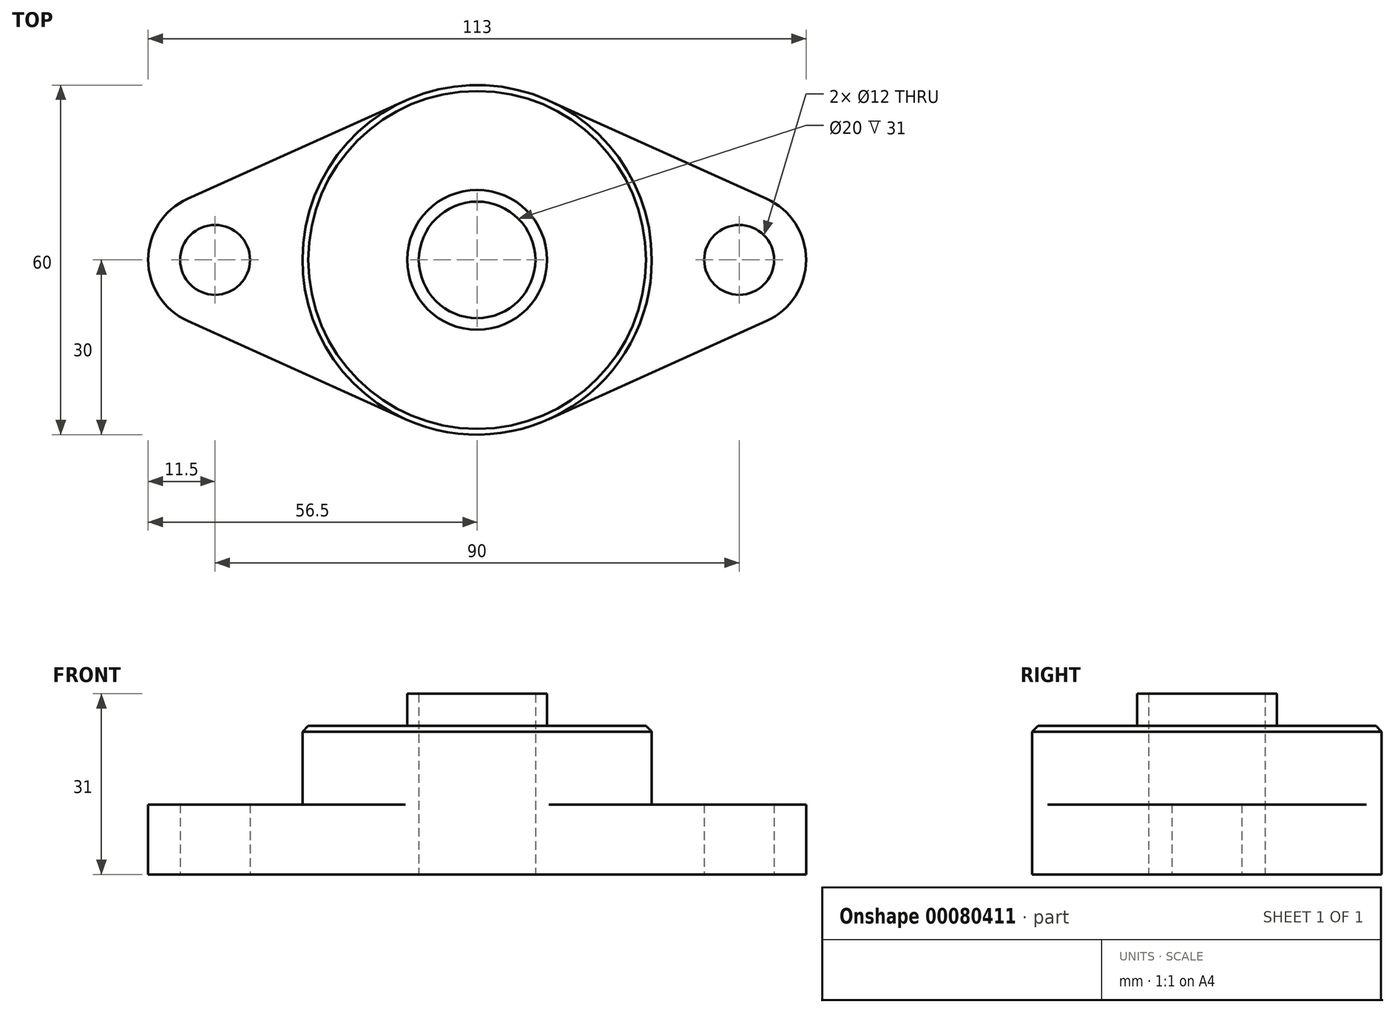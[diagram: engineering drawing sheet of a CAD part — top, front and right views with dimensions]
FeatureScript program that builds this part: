
annotation { "Feature Type Name" : "Feature", "Feature Type Description" : "" }
export const myFeature = defineFeature(function(context is Context, id is Id, definition is map)
    precondition{}
    {
        {
            var Q0;
            Q0=qCreatedBy(makeId("Top.planeOp"),FACE);
            var sketch = newSketch(context, id + "F0", { "sketchPlane" : qUnion([Q0])});
            skCircle(sketch, "E0", {"center": v(0, 0) * mm, "radius": 10 * mm});
            skArc(sketch, "E1", {"start": v(-49.73, 10.48) * mm, "mid": v(-56.5, 0) * mm, "end": v(-49.73, -10.48) * mm});
            skArc(sketch, "E2", {"start": v(-12.33, -27.35) * mm, "mid": v(0, -30) * mm, "end": v(12.33, -27.35) * mm});
            skLineSegment(sketch, "E3", {"start": v(-49.73, 10.48) * mm, "end": v(-12.33, 27.35) * mm});
            skLineSegment(sketch, "E4.MirrorCS", {"start": v(-49.73, -10.48) * mm, "end": v(-12.33, -27.35) * mm});
            skCircle(sketch, "E5", {"center": v(-45, 0) * mm, "radius": 6 * mm});
            skLineSegment(sketch, "E6.MirrorCS", {"start": v(49.73, 10.48) * mm, "end": v(12.33, 27.35) * mm});
            skArc(sketch, "E7.MirrorCS", {"start": v(49.73, 10.48) * mm, "mid": v(56.5, 0) * mm, "end": v(49.73, -10.48) * mm});
            skLineSegment(sketch, "E8.MirrorCS", {"start": v(49.73, -10.48) * mm, "end": v(12.33, -27.35) * mm});
            skCircle(sketch, "E9.MirrorC", {"center": v(45, 0) * mm, "radius": 6 * mm});
            skArc(sketch, "E10.trimOffspring", {"start": v(12.33, 27.35) * mm, "mid": v(0, 30) * mm, "end": v(-12.33, 27.35) * mm});
            skPoint(sketch, "E11", {"position": v(0, 30) * mm});
            skPoint(sketch, "E12", {"position": v(0, -30) * mm});
            skSolve(sketch);
        }
        {
            var Q0;
            Q0 = qSketchRegion(id + "F0", true);
            extrude(context, id + "F1", {"entities" : qUnion([Q0]), "endBound" : BoundingType.SYMMETRIC, "depth" : 12 * mm});
        }
        {
            var Q0;
            Q0=makeQuery(id+"F1.opExtrude","CAP_FACE",FACE,{"disambiguationData":[OSD([sQuery(id+"F0.wireOp",EDGE,"E0"),sQuery(id+"F0.wireOp",EDGE,"E1"),sQuery(id+"F0.wireOp",EDGE,"E2"),sQuery(id+"F0.wireOp",EDGE,"E3"),sQuery(id+"F0.wireOp",EDGE,"E4.MirrorCS"),sQuery(id+"F0.wireOp",EDGE,"E5"),sQuery(id+"F0.wireOp",EDGE,"E6.MirrorCS"),sQuery(id+"F0.wireOp",EDGE,"E7.MirrorCS"),sQuery(id+"F0.wireOp",EDGE,"E8.MirrorCS"),sQuery(id+"F0.wireOp",EDGE,"E9.MirrorC"),sQuery(id+"F0.wireOp",EDGE,"E10.trimOffspring")])],"isStart":false});
            var sketch = newSketch(context, id + "F2", { "sketchPlane" : qUnion([Q0])});
            skCircle(sketch, "E13", {"center": v(0, 0) * mm, "radius": 30 * mm});
            skCircle(sketch, "E14.0", {"center": v(0, 0) * mm, "radius": 10 * mm});
            skSolve(sketch);
        }
        {
            var Q0;
            Q0 = qSketchRegion(id + "F2", true);
            extrude(context, id + "F3", {"entities" : qUnion([Q0]), "operationType" : NewBodyOperationType.ADD, "depth" : (25.5 - 12) * mm});
        }
        {
            var Q0;
            Q0=makeQuery(id+"F3.opExtrude","CAP_FACE",FACE,{"disambiguationData":[OSD([sQuery(id+"F2.wireOp",EDGE,"E13"),sQuery(id+"F2.wireOp",EDGE,"E14.0")])],"isStart":false});
            var sketch = newSketch(context, id + "F4", { "sketchPlane" : qUnion([Q0])});
            skCircle(sketch, "E15", {"center": v(0, 0) * mm, "radius": 12 * mm});
            skCircle(sketch, "E16.0", {"center": v(0, 0) * mm, "radius": 10 * mm});
            skPoint(sketch, "E17", {"position": v(0, 12) * mm});
            skPoint(sketch, "E18", {"position": v(0, 10) * mm});
            skSolve(sketch);
        }
        {
            var Q0;
            Q0 = qSketchRegion(id + "F4", true);
            extrude(context, id + "F5", {"entities" : qUnion([Q0]), "operationType" : NewBodyOperationType.ADD, "depth" : (31 - 25.5) * mm});
        }
        {
            var Q0;
            Q0=makeQuery(id+"F3.opExtrude","CAP_EDGE",EDGE,{"disambiguationData":[OSD([sQuery(id+"F2.wireOp",EDGE,"E13")])],"isStart":false});
            chamfer(context, id + "F6", {"entities" : qUnion([Q0]), "width" : 1 * mm, "tangentPropagation" : true});
        }
    });
